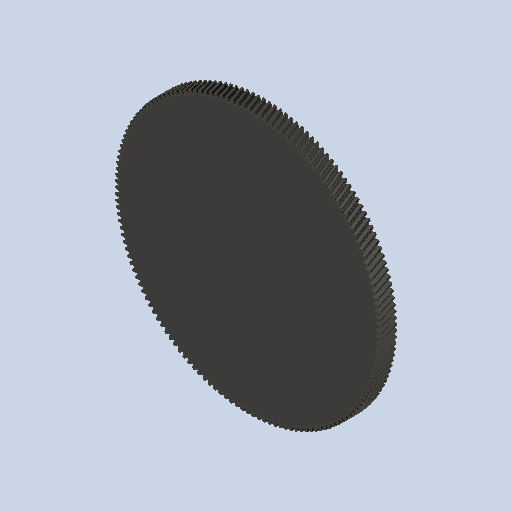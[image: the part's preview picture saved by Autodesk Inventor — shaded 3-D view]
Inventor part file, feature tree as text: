
AUTODESK INVENTOR PART (.ipt)
format: ipt  version: 2023 (Build 270158000, 158)  size: 1,716,736 bytes
history: native  units: mm (DEFAULTED — no unit token found)
features: plane x3, other x3, sketch x2, extrude x1
ambient origin geometry x8: Origin, YZ Plane, XZ Plane, XY Plane, X Axis, Y Axis, Z Axis, Center Point
bodies: Solid1 (feature_tree)
feature tree (9):
  extrude  "Extrusion1"  Depth=10.0mm TaperAngle=0.0deg
  plane  "Work Plane2"
  plane  "Work Plane8"
  plane  "Work Plane9"
  other  "Spur Gear"
  sketch  "Sketch1"  dims[d0=161.626666mm d1=10.0mm d2=0.0mm]
  sketch  "Sketch2"  dims[d3=159.626666mm d4=10.0mm d5=0.0mm d16=80.0mm d17=0.0mm d34=0.20944mm d39=0.0mm d41=0.0mm d43=80.0mm d46=80.0mm d47=0.0mm d48=0.0mm]
  other  "Srf1"
  other  "Pitch Diameter"
